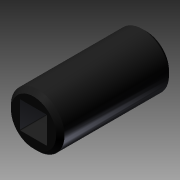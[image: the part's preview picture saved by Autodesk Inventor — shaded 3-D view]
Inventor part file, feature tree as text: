
AUTODESK INVENTOR PART (.ipt)
format: ipt  version: 2013 (Build 170138000, 138)  size: 124,928 bytes
history: native  units: in
note: dims shown in document units (in); Inventor stores cm internally (conversion verified against a paired STEP export)
features: extrude x5, sketch x5, chamfer x1, other x1
ambient origin geometry x8: Origin, YZ Plane, XZ Plane, XY Plane, X Axis, Y Axis, Z Axis, Center Point
bodies: Solid1 (feature_tree)
feature tree (12):
  extrude  "Extrusion1"  Depth=0.5315in TaperAngle=0.0deg
  extrude  "Extrusion2"  Depth=0.2126in TaperAngle=0.0deg
  extrude  "Extrusion3"  Depth=0.2874in TaperAngle=0.0deg
  extrude  "Extrusion4"  Depth=0.3937in TaperAngle=0.0deg
  chamfer  "Chamfer1"  [1 undecoded]
  sketch  "Sketch1"  dims[d0=0.252in d1=0.5315in d2=0.0in]
  sketch  "Sketch2"  dims[d3=0.2264in d4=0.0in d5=0.2126in d6=0.0in]
  sketch  "Sketch3"  dims[d7=0.125in d8=0.2874in d9=0.0in]
  sketch  "Sketch4"  dims[d10=0.0197in d11=0.0787in d12=45.0deg d13=0.3937in d14=0.0in]
  sketch  "Sketch5"  dims[d15=0.0in d16=0.0in]
  other  "Srf1"
  extrude  "ExtrusionSrf1"  [1 undecoded]
note: 2 required parameter values undecoded (feature->parameter linkage not recoverable at this tier; creation-order binding heuristic only, values carry confidence <= 0.55)
